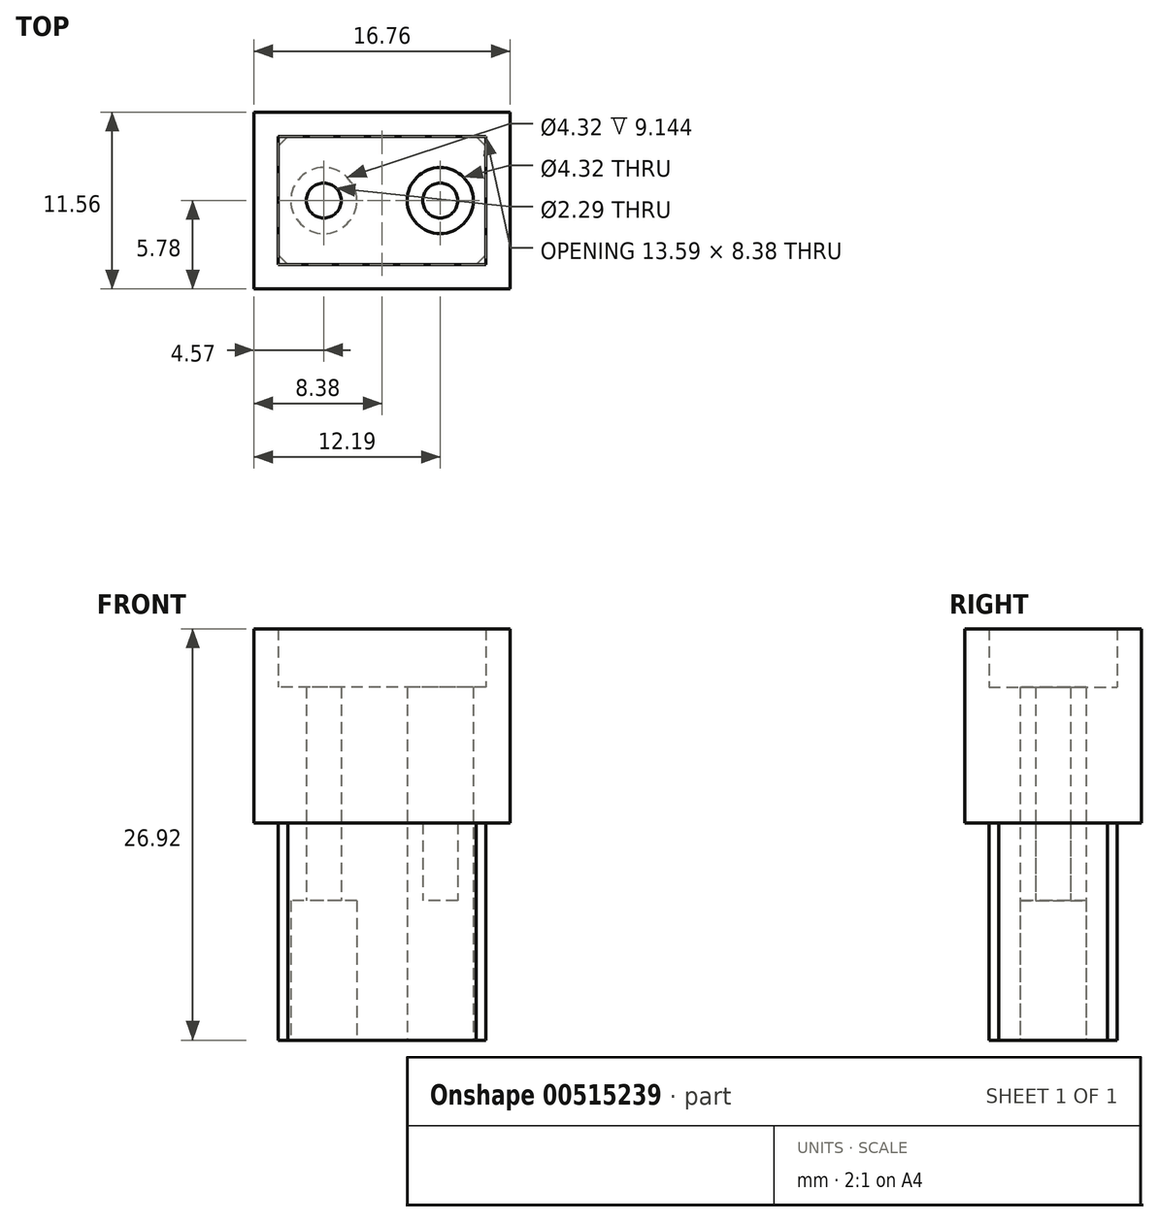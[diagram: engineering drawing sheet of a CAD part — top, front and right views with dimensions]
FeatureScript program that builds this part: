
annotation { "Feature Type Name" : "Feature", "Feature Type Description" : "" }
export const myFeature = defineFeature(function(context is Context, id is Id, definition is map)
    precondition{}
    {
        {
            var Q0;
            Q0=qCreatedBy(makeId("Top.planeOp"),FACE);
            var sketch = newSketch(context, id + "F0", { "sketchPlane" : qUnion([Q0])});
            skLineSegment(sketch, "E0.bottom", {"start": v(6.8, 4.2) * mm, "end": v(-6.8, 4.2) * mm});
            skLineSegment(sketch, "E0.top", {"start": v(6.8, -4.2) * mm, "end": v(-6.8, -4.2) * mm});
            skLineSegment(sketch, "E0.left", {"start": v(6.8, 4.2) * mm, "end": v(6.8, -4.2) * mm});
            skLineSegment(sketch, "E0.right", {"start": v(-6.8, 4.2) * mm, "end": v(-6.8, -4.2) * mm});
            skPoint(sketch, "E0.middle", {"position": v(0, 0) * mm});
            skCircle(sketch, "E1", {"center": v(-3.81, 0) * mm, "radius": 2.16 * mm});
            skCircle(sketch, "E2.MirrorC", {"center": v(3.81, 0) * mm, "radius": 2.16 * mm});
            skSolve(sketch);
        }
        {
            var Q0;
            Q0=makeQuery(id+"F0.imprint","IMPRINT",FACE,{"disambiguationData":[TD([[makeQuery(id+"F0.imprint","IMPRINT",EDGE,{"derivedFrom":sQuery(id+"F0.wireOp",EDGE,"E0.bottom")}),1.0]])]});
            extrude(context, id + "F1", {"entities" : qUnion([Q0]), "depth" : 9.14 * mm, "offsetDistance" : 25.4 * mm});
        }
        {
            var Q0;
            Q0=makeQuery(id+"F1.opExtrude","CAP_FACE",FACE,{"disambiguationData":[OSD([sQuery(id+"F0.wireOp",EDGE,"E0.bottom"),sQuery(id+"F0.wireOp",EDGE,"E0.top"),sQuery(id+"F0.wireOp",EDGE,"E0.left"),sQuery(id+"F0.wireOp",EDGE,"E0.right"),sQuery(id+"F0.wireOp",EDGE,"E1"),sQuery(id+"F0.wireOp",EDGE,"E2.MirrorC")])],"isStart":false});
            var sketch = newSketch(context, id + "F2", { "sketchPlane" : qUnion([Q0])});
            skCircle(sketch, "E3", {"center": v(-3.81, 0) * mm, "radius": 1.14 * mm});
            skCircle(sketch, "E4.MirrorC", {"center": v(3.81, 0) * mm, "radius": 1.14 * mm});
            skSolve(sketch);
        }
        {
            var Q0;
            Q0=makeQuery(id+"F2.imprint","IMPRINT",FACE,{"disambiguationData":[TD([[makeQuery(id+"F2.imprint","IMPRINT",EDGE,{"derivedFrom":makeQuery(id+"F1.opExtrude","CAP_EDGE",EDGE,{"disambiguationData":[OSD([sQuery(id+"F0.wireOp",EDGE,"E0.bottom")])],"isStart":false})}),1.0]])]});
            var Q1;
            Q1=makeQuery(id+"F2.imprint","IMPRINT",FACE,{"disambiguationData":[TD([[makeQuery(id+"F2.imprint","IMPRINT",EDGE,{"derivedFrom":sQuery(id+"F2.wireOp",EDGE,"E3")}),-1.0]])]});
            var Q2;
            Q2=makeQuery(id+"F2.imprint","IMPRINT",FACE,{"disambiguationData":[TD([[makeQuery(id+"F2.imprint","IMPRINT",EDGE,{"derivedFrom":sQuery(id+"F2.wireOp",EDGE,"E4.MirrorC")}),1.0]])]});
            extrude(context, id + "F3", {"entities" : qUnion([Q0, Q1, Q2]), "operationType" : NewBodyOperationType.ADD, "depth" : 5.08 * mm, "offsetDistance" : 25.4 * mm});
        }
        {
            var Q0;
            Q0=makeQuery(id+"F3.opExtrude","CAP_FACE",FACE,{"disambiguationData":[OSD([sQuery(id+"F0.wireOp",EDGE,"E0.bottom"),sQuery(id+"F0.wireOp",EDGE,"E0.top"),sQuery(id+"F0.wireOp",EDGE,"E0.left"),sQuery(id+"F0.wireOp",EDGE,"E0.right"),sQuery(id+"F2.wireOp",EDGE,"E3"),sQuery(id+"F2.wireOp",EDGE,"E4.MirrorC")])],"isStart":false});
            var sketch = newSketch(context, id + "F4", { "sketchPlane" : qUnion([Q0])});
            skLineSegment(sketch, "E5.bottom", {"start": v(-8.38, 5.78) * mm, "end": v(8.38, 5.78) * mm});
            skLineSegment(sketch, "E5.top", {"start": v(-8.38, -5.78) * mm, "end": v(8.38, -5.78) * mm});
            skLineSegment(sketch, "E5.left", {"start": v(-8.38, 5.78) * mm, "end": v(-8.38, -5.78) * mm});
            skLineSegment(sketch, "E5.right", {"start": v(8.38, 5.78) * mm, "end": v(8.38, -5.78) * mm});
            skPoint(sketch, "E5.middle", {"position": v(0, 0) * mm});
            skSolve(sketch);
        }
        {
            var Q0;
            Q0=makeQuery(id+"F4.imprint","IMPRINT",FACE,{"disambiguationData":[TD([[makeQuery(id+"F4.imprint","IMPRINT",EDGE,{"derivedFrom":makeQuery(id+"F3.opExtrude","CAP_EDGE",EDGE,{"disambiguationData":[OSD([sQuery(id+"F2.wireOp",EDGE,"E3")])],"isStart":false})}),-1.0]])]});
            var Q1;
            Q1=makeQuery(id+"F4.imprint","IMPRINT",FACE,{"disambiguationData":[TD([[makeQuery(id+"F4.imprint","IMPRINT",EDGE,{"derivedFrom":sQuery(id+"F4.wireOp",EDGE,"E5.bottom")}),-1.0]])]});
            extrude(context, id + "F5", {"entities" : qUnion([Q0, Q1]), "operationType" : NewBodyOperationType.ADD, "depth" : 8.9 * mm, "offsetDistance" : 25.4 * mm});
        }
        {
            var Q0;
            {var subQ0=sQuery(id+"F0.wireOp",EDGE,"E0.right");var subQ1=sQuery(id+"F0.wireOp",EDGE,"E0.bottom");Q0=makeQuery(id+"F3.boolean.opBoolean","MERGE",EDGE,{"derivedFrom":[makeQuery(id+"F1.opExtrude","SWEPT_EDGE",EDGE,{"disambiguationData":[OSD([subQ1,subQ0])]}),makeQuery(id+"F3.opExtrude","SWEPT_EDGE",EDGE,{"disambiguationData":[OSD([subQ1,subQ0])]})]});}
            var Q1;
            {var subQ0=sQuery(id+"F0.wireOp",EDGE,"E0.right");var subQ1=sQuery(id+"F0.wireOp",EDGE,"E0.top");Q1=makeQuery(id+"F3.boolean.opBoolean","MERGE",EDGE,{"derivedFrom":[makeQuery(id+"F1.opExtrude","SWEPT_EDGE",EDGE,{"disambiguationData":[OSD([subQ1,subQ0])]}),makeQuery(id+"F3.opExtrude","SWEPT_EDGE",EDGE,{"disambiguationData":[OSD([subQ1,subQ0])]})]});}
            var Q2;
            {var subQ0=sQuery(id+"F0.wireOp",EDGE,"E0.left");var subQ1=sQuery(id+"F0.wireOp",EDGE,"E0.bottom");Q2=makeQuery(id+"F3.boolean.opBoolean","MERGE",EDGE,{"derivedFrom":[makeQuery(id+"F1.opExtrude","SWEPT_EDGE",EDGE,{"disambiguationData":[OSD([subQ1,subQ0])]}),makeQuery(id+"F3.opExtrude","SWEPT_EDGE",EDGE,{"disambiguationData":[OSD([subQ1,subQ0])]})]});}
            var Q3;
            {var subQ0=sQuery(id+"F0.wireOp",EDGE,"E0.left");var subQ1=sQuery(id+"F0.wireOp",EDGE,"E0.top");Q3=makeQuery(id+"F3.boolean.opBoolean","MERGE",EDGE,{"derivedFrom":[makeQuery(id+"F1.opExtrude","SWEPT_EDGE",EDGE,{"disambiguationData":[OSD([subQ1,subQ0])]}),makeQuery(id+"F3.opExtrude","SWEPT_EDGE",EDGE,{"disambiguationData":[OSD([subQ1,subQ0])]})]});}
            chamfer(context, id + "F6", {"entities" : qUnion([Q0, Q1, Q2, Q3]), "width" : 0.64 * mm, "tangentPropagation" : true});
        }
        {
            var Q0;
            Q0=makeQuery(id+"F5.opExtrude","CAP_FACE",FACE,{"disambiguationData":[OSD([sQuery(id+"F2.wireOp",EDGE,"E3"),sQuery(id+"F2.wireOp",EDGE,"E4.MirrorC"),sQuery(id+"F4.wireOp",EDGE,"E5.bottom"),sQuery(id+"F4.wireOp",EDGE,"E5.top"),sQuery(id+"F4.wireOp",EDGE,"E5.left"),sQuery(id+"F4.wireOp",EDGE,"E5.right")])],"isStart":false});
            var sketch = newSketch(context, id + "F7", { "sketchPlane" : qUnion([Q0])});
            skLineSegment(sketch, "E6.bottom", {"start": v(6.8, -4.2) * mm, "end": v(-6.8, -4.2) * mm});
            skLineSegment(sketch, "E6.top", {"start": v(6.8, 4.2) * mm, "end": v(-6.8, 4.2) * mm});
            skLineSegment(sketch, "E6.left", {"start": v(6.8, -4.2) * mm, "end": v(6.8, 4.2) * mm});
            skLineSegment(sketch, "E6.right", {"start": v(-6.8, -4.2) * mm, "end": v(-6.8, 4.2) * mm});
            skPoint(sketch, "E6.middle", {"position": v(0, 0) * mm});
            skSolve(sketch);
        }
        {
            var Q0;
            Q0=makeQuery(id+"F7.imprint","IMPRINT",FACE,{"disambiguationData":[TD([[makeQuery(id+"F7.imprint","IMPRINT",EDGE,{"derivedFrom":sQuery(id+"F7.wireOp",EDGE,"E6.bottom")}),1.0]])]});
            extrude(context, id + "F8", {"entities" : qUnion([Q0]), "operationType" : NewBodyOperationType.ADD, "depth" : 3.8 * mm, "offsetDistance" : 25.4 * mm});
        }
    });
